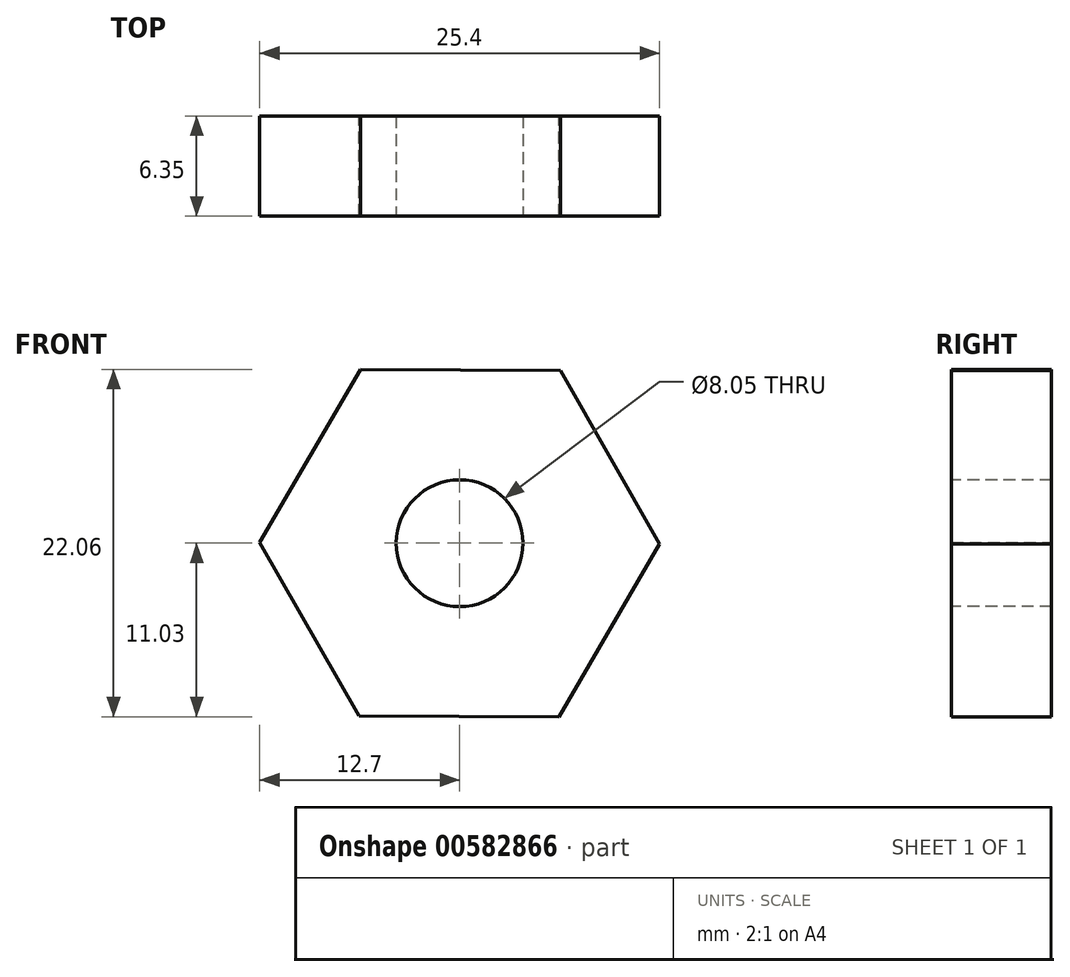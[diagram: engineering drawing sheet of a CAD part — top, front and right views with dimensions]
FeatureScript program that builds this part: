
annotation { "Feature Type Name" : "Feature", "Feature Type Description" : "" }
export const myFeature = defineFeature(function(context is Context, id is Id, definition is map)
    precondition{}
    {
        {
            var Q0;
            Q0=qCreatedBy(makeId("Front.planeOp"),FACE);
            var sketch = newSketch(context, id + "F0", { "sketchPlane" : qUnion([Q0])});
            skCircle(sketch, "E0.cCircle", {"center": v(0, 0) * mm, "radius": 11 * mm, "construction": true});
            skLineSegment(sketch, "E0.0", {"start": v(12.7, -0.06) * mm, "end": v(6.3, -11.03) * mm});
            skLineSegment(sketch, "E0.1", {"start": v(6.3, -11.03) * mm, "end": v(-6.4, -10.97) * mm});
            skLineSegment(sketch, "E0.2", {"start": v(-6.4, -10.97) * mm, "end": v(-12.7, 0.06) * mm});
            skLineSegment(sketch, "E0.3", {"start": v(-12.7, 0.06) * mm, "end": v(-6.3, 11.03) * mm});
            skLineSegment(sketch, "E0.4", {"start": v(-6.3, 11.03) * mm, "end": v(6.4, 10.97) * mm});
            skLineSegment(sketch, "E0.5", {"start": v(6.4, 10.97) * mm, "end": v(12.7, -0.06) * mm});
            skPoint(sketch, "E0.0.midPoint", {"position": v(9.5, -5.54) * mm});
            skSolve(sketch);
        }
        {
            var Q0;
            Q0 = qSketchRegion(id + "F0", true);
            extrude(context, id + "F1", {"entities" : qUnion([Q0]), "depth" : 6.35 * mm, "offsetDistance" : 25.4 * mm});
        }
        {
            var Q0;
            Q0=makeQuery(id+"F1.opExtrude","CAP_FACE",FACE,{"disambiguationData":[OSD([sQuery(id+"F0.wireOp",EDGE,"E0.0"),sQuery(id+"F0.wireOp",EDGE,"E0.1"),sQuery(id+"F0.wireOp",EDGE,"E0.2"),sQuery(id+"F0.wireOp",EDGE,"E0.3"),sQuery(id+"F0.wireOp",EDGE,"E0.4"),sQuery(id+"F0.wireOp",EDGE,"E0.5")])],"isStart":false});
            var sketch = newSketch(context, id + "F2", { "sketchPlane" : qUnion([Q0])});
            skCircle(sketch, "E1", {"center": v(0, 0) * mm, "radius": 4.03 * mm});
            skSolve(sketch);
        }
        {
            var Q0;
            Q0 = qSketchRegion(id + "F2", true);
            extrude(context, id + "F3", {"entities" : qUnion([Q0]), "operationType" : NewBodyOperationType.REMOVE, "oppositeDirection" : true, "depth" : 25.4 * mm, "offsetDistance" : 25.4 * mm});
        }
    });
